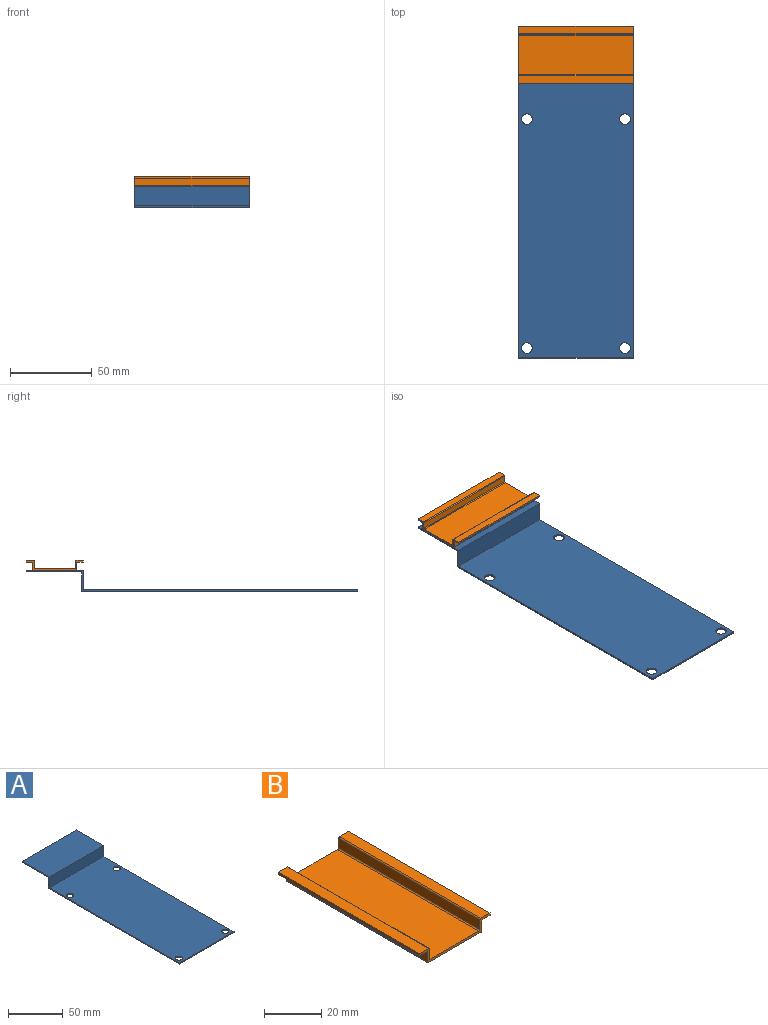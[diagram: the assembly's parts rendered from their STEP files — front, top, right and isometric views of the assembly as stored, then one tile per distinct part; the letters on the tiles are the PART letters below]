
ASSEMBLY  parts=2 mates=1
PART A: 14 faces, bbox 70x203x13 mm
  f0: plane 169x70mm, normal (0,0,-1), area 11697.3mm2, adj f1,f2,f3,f8,f10,f11,f12,f13
  f1: plane 203x13mm, normal (-1,0,0), area 215mm2, adj f0,f2,f4,f5,f6,f7,f8,f9
  f2: plane 70x1mm, normal (0,-1,0), area 70mm2, adj f0,f1,f3,f4
  f3: plane 203x13mm, normal (1,0,0), area 215mm2, adj f0,f2,f4,f5,f6,f7,f8,f9
  f4: plane 168x70mm, normal (0,0,1), area 11627.3mm2, adj f1,f2,f3,f5,f10,f11,f12,f13
  f5: plane 70x12mm, normal (0,-1,0), area 840mm2, adj f1,f3,f4,f7
  f6: plane 70x1mm, normal (0,1,0), area 70mm2, adj f1,f3,f7,f9
  f7: plane 70x35mm, normal (0,0,1), area 2450mm2, adj f1,f3,f5,f6
  f8: plane 70x12mm, normal (0,1,0), area 840mm2, adj f0,f1,f3,f9
  f9: plane 70x34mm, normal (0,0,-1), area 2380mm2, adj f1,f3,f6,f8
  f10: cylinder r=3.25mm len=6.5mm, axis (0,0,1), area 20.4mm2, adj f0,f4
  f11: cylinder r=3.25mm len=6.5mm, axis (0,0,1), area 20.4mm2, adj f0,f4
  f12: cylinder r=3.25mm len=6.5mm, axis (0,0,1), area 20.4mm2, adj f0,f4
  f13: cylinder r=3.25mm len=6.5mm, axis (0,0,1), area 20.4mm2, adj f0,f4
PART B: 20 faces, bbox 35x70x6 mm
  f0: plane 70x4.5mm, normal (1,0,0), area 315mm2, adj f1,f12,f13,f19
  f1: plane 70x4mm, normal (0,0,-1), area 280mm2, adj f0,f2,f12,f13
  f2: plane 70x1mm, normal (1,0,0), area 70mm2, adj f1,f3,f12,f13
  f3: plane 70x4.5mm, normal (0,0,1), area 315mm2, adj f2,f12,f13,f14
  f4: plane 70x4mm, normal (-1,0,0), area 280mm2, adj f12,f13,f14,f15
  f5: plane 70x24mm, normal (0,0,1), area 1680mm2, adj f12,f13,f15,f16
  f6: plane 70x4mm, normal (1,0,0), area 280mm2, adj f12,f13,f16,f17
  f7: plane 70x4.5mm, normal (0,0,1), area 315mm2, adj f8,f12,f13,f17
  f8: plane 70x1mm, normal (-1,0,0), area 70mm2, adj f7,f9,f12,f13
  f9: plane 70x4mm, normal (0,0,-1), area 280mm2, adj f8,f10,f12,f13
  f10: plane 70x4.5mm, normal (-1,0,0), area 315mm2, adj f9,f12,f13,f18
  f11: plane 70x26mm, normal (0,0,-1), area 1820mm2, adj f12,f13,f18,f19
  f12: plane 35x6mm, normal (0,-1,0), area 44.9mm2, adj f0,f1,f2,f3,f4,f5,f6,f7
  f13: plane 35x6mm, normal (0,1,0), area 44.9mm2, adj f0,f1,f2,f3,f4,f5,f6,f7
  f14: cylinder r=0.5mm len=70mm, axis (0,1,0), area 55mm2, adj f3,f4,f12,f13
  f15: cylinder r=0.5mm len=70mm, axis (0,-1,0), area 55mm2, adj f4,f5,f12,f13
  f16: cylinder r=0.5mm len=70mm, axis (0,1,0), area 55mm2, adj f5,f6,f12,f13
  f17: cylinder r=0.5mm len=70mm, axis (0,-1,0), area 55mm2, adj f6,f7,f12,f13
  f18: cylinder r=0.5mm len=70mm, axis (0,-1,0), area 55mm2, adj f10,f11,f12,f13
  f19: cylinder r=0.5mm len=70mm, axis (0,1,0), area 55mm2, adj f0,f11,f12,f13
PLACE A t=(-36.1,-173.36,-52.75)mm
PLACE B rot(axis=(0,0,1),90deg) t=(-35.6,-79.32,-37.25)mm
MATE fastened B.f11 <-> A.f7  axis (0,0,-1) through (-35.6,-79.32,-39.75)mm
